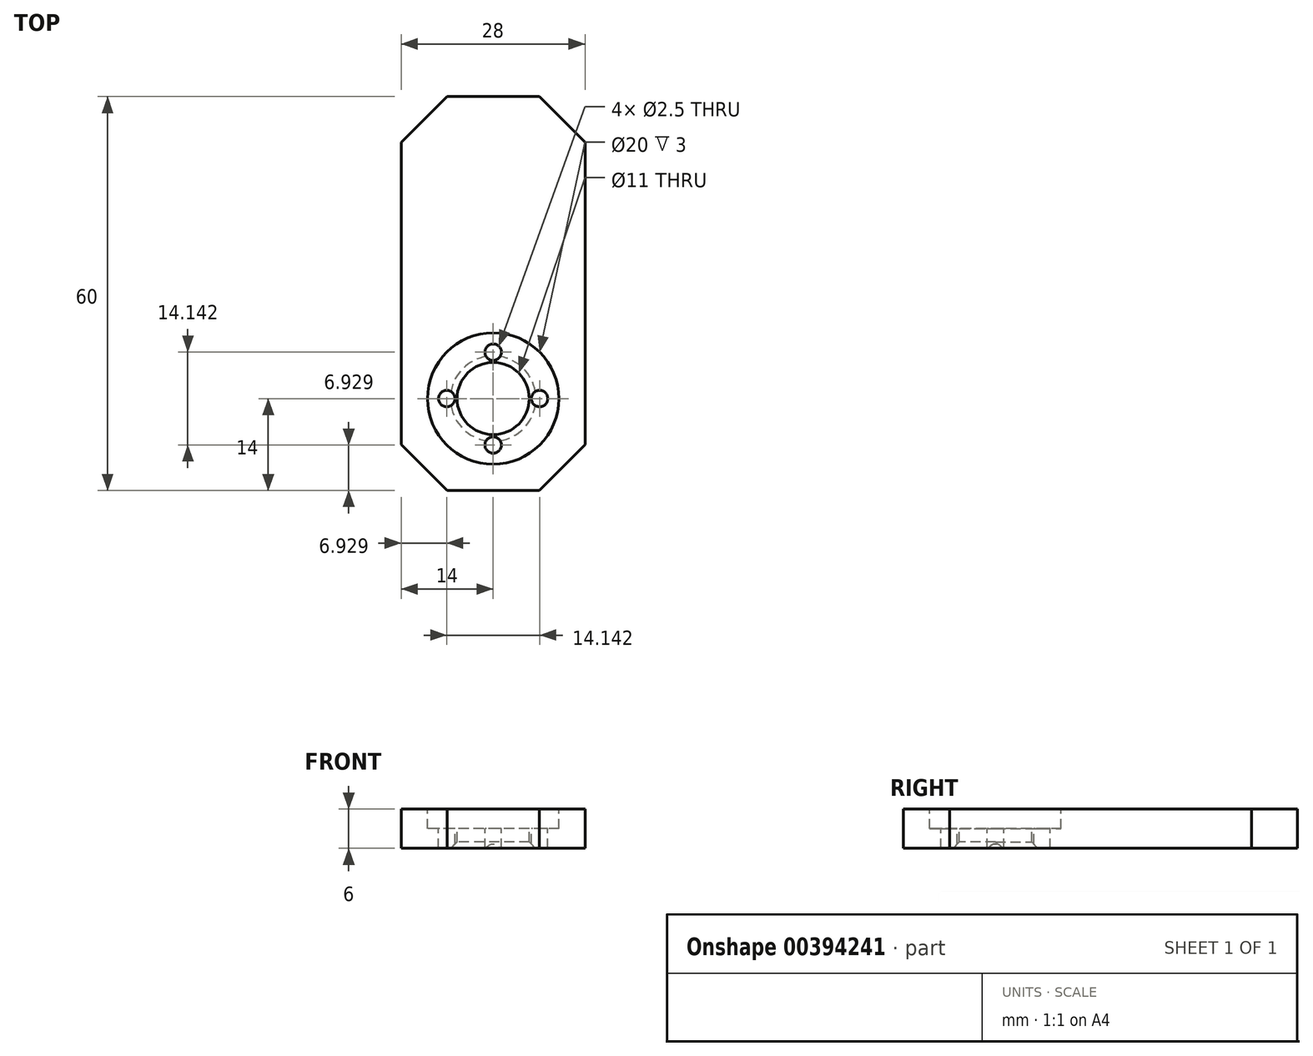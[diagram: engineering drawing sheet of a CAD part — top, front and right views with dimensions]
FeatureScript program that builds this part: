
annotation { "Feature Type Name" : "Feature", "Feature Type Description" : "" }
export const myFeature = defineFeature(function(context is Context, id is Id, definition is map)
    precondition{}
    {
        {
            var Q0;
            Q0=qCreatedBy(makeId("Top.planeOp"),FACE);
            var sketch = newSketch(context, id + "F0", { "sketchPlane" : qUnion([Q0])});
            skLineSegment(sketch, "E0.bottom", {"start": v(-14, 46) * mm, "end": v(14, 46) * mm});
            skLineSegment(sketch, "E0.top", {"start": v(-14, -14) * mm, "end": v(14, -14) * mm});
            skLineSegment(sketch, "E0.left", {"start": v(-14, 46) * mm, "end": v(-14, -14) * mm});
            skLineSegment(sketch, "E0.right", {"start": v(14, 46) * mm, "end": v(14, -14) * mm});
            skLineSegment(sketch, "E1", {"start": v(0, 50.42) * mm, "end": v(0, -18.38) * mm, "construction": true});
            skLineSegment(sketch, "E2", {"start": v(-18.38, 0) * mm, "end": v(19.17, 0) * mm, "construction": true});
            skSolve(sketch);
        }
        {
            var Q0;
            Q0=qSketchRegion(id+"F0",true);
            extrude(context, id + "F1", {"entities" : qUnion([Q0]), "depth" : 6 * mm, "offsetDistance" : 25 * mm});
        }
        {
            var Q0;
            Q0=makeQuery(id+"F1.opExtrude","CAP_FACE",FACE,{"disambiguationData":[OSD([sQuery(id+"F0.wireOp",EDGE,"E0.bottom"),sQuery(id+"F0.wireOp",EDGE,"E0.top"),sQuery(id+"F0.wireOp",EDGE,"E0.left"),sQuery(id+"F0.wireOp",EDGE,"E0.right")])],"isStart":false});
            var sketch = newSketch(context, id + "F2", { "sketchPlane" : qUnion([Q0])});
            skCircle(sketch, "E3", {"center": v(0, 0) * mm, "radius": 10 * mm});
            skSolve(sketch);
        }
        {
            var Q0;
            Q0=qSketchRegion(id+"F2",true);
            extrude(context, id + "F3", {"entities" : qUnion([Q0]), "operationType" : NewBodyOperationType.REMOVE, "oppositeDirection" : true, "depth" : 3 * mm, "offsetDistance" : 25 * mm});
        }
        {
            var Q0;
            Q0=makeQuery(id+"F3.boolean.opBoolean","COPY",FACE,{"derivedFrom":makeQuery(id+"F3.opExtrude","CAP_FACE",FACE,{"disambiguationData":[OSD([sQuery(id+"F2.wireOp",EDGE,"E3")])],"isStart":false})});
            var sketch = newSketch(context, id + "F4", { "sketchPlane" : qUnion([Q0])});
            skCircle(sketch, "E4", {"center": v(0, 0) * mm, "radius": 5.5 * mm});
            skCircle(sketch, "E5", {"center": v(0, 0) * mm, "radius": 7.07 * mm, "construction": true});
            skCircle(sketch, "E6", {"center": v(0, 7.07) * mm, "radius": 1.25 * mm});
            skCircle(sketch, "E7.1.0", {"center": v(7.07, 0) * mm, "radius": 1.25 * mm});
            skCircle(sketch, "E7.2.0", {"center": v(0, -7.07) * mm, "radius": 1.25 * mm});
            skLineSegment(sketch, "E7.anchor1", {"start": v(0, 0) * mm, "end": v(0, 7.07) * mm, "construction": true});
            skLineSegment(sketch, "E7.anchor2", {"start": v(0, 0) * mm, "end": v(-7.07, 0) * mm, "construction": true});
            skCircle(sketch, "E8.1.3.0", {"center": v(-7.07, 0) * mm, "radius": 1.25 * mm});
            skSolve(sketch);
        }
        {
            var Q0;
            Q0=qSketchRegion(id+"F4",true);
            extrude(context, id + "F5", {"entities" : qUnion([Q0]), "operationType" : NewBodyOperationType.REMOVE, "endBound" : BoundingType.THROUGH_ALL, "oppositeDirection" : true, "depth" : 25 * mm, "offsetDistance" : 25 * mm});
        }
        {
            var Q0;
            Q0=makeQuery(id+"F5.boolean.opBoolean","INTERSECT",EDGE,{"derivedFrom":[makeQuery(id+"F1.opExtrude","CAP_FACE",FACE,{"disambiguationData":[OSD([sQuery(id+"F0.wireOp",EDGE,"E0.bottom"),sQuery(id+"F0.wireOp",EDGE,"E0.top"),sQuery(id+"F0.wireOp",EDGE,"E0.left"),sQuery(id+"F0.wireOp",EDGE,"E0.right")])],"isStart":true}),makeQuery(id+"F5.opExtrude","SWEPT_FACE",FACE,{"disambiguationData":[OSD([sQuery(id+"F4.wireOp",EDGE,"E4")])]})]});
            chamfer(context, id + "F6", {"entities" : qUnion([Q0]), "width" : 1 * mm, "tangentPropagation" : true});
        }
        {
            var Q0;
            Q0=makeQuery(id+"F1.opExtrude","SWEPT_EDGE",EDGE,{"disambiguationData":[OSD([sQuery(id+"F0.wireOp",EDGE,"E0.top"),sQuery(id+"F0.wireOp",EDGE,"E0.right")])]});
            var Q1;
            Q1=makeQuery(id+"F1.opExtrude","SWEPT_EDGE",EDGE,{"disambiguationData":[OSD([sQuery(id+"F0.wireOp",EDGE,"E0.top"),sQuery(id+"F0.wireOp",EDGE,"E0.left")])]});
            var Q2;
            Q2=makeQuery(id+"F1.opExtrude","SWEPT_EDGE",EDGE,{"disambiguationData":[OSD([sQuery(id+"F0.wireOp",EDGE,"E0.bottom"),sQuery(id+"F0.wireOp",EDGE,"E0.right")])]});
            var Q3;
            Q3=makeQuery(id+"F1.opExtrude","SWEPT_EDGE",EDGE,{"disambiguationData":[OSD([sQuery(id+"F0.wireOp",EDGE,"E0.bottom"),sQuery(id+"F0.wireOp",EDGE,"E0.left")])]});
            chamfer(context, id + "F7", {"entities" : qUnion([Q0, Q1, Q2, Q3]), "width" : 7 * mm, "tangentPropagation" : true});
        }
    });
